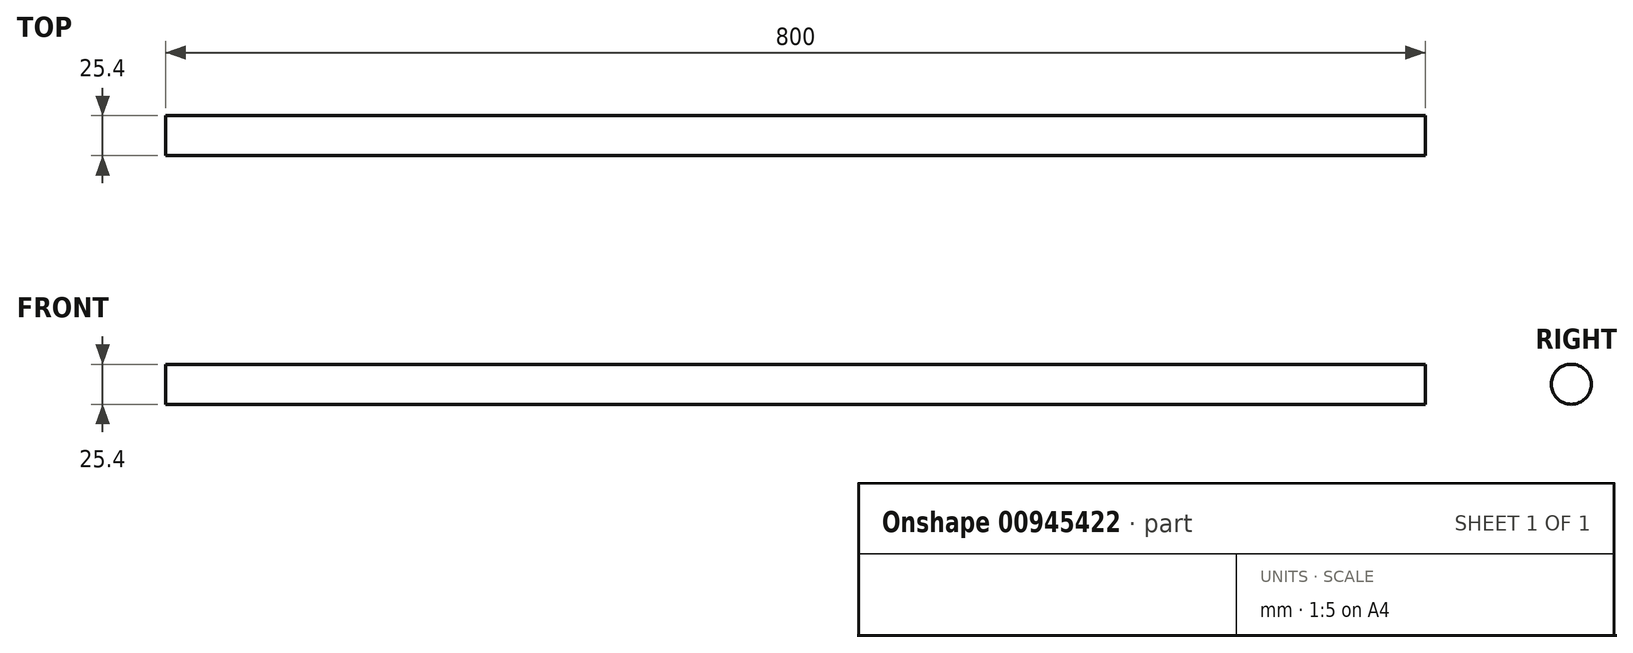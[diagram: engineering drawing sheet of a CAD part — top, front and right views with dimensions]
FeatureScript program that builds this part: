
annotation { "Feature Type Name" : "Feature", "Feature Type Description" : "" }
export const myFeature = defineFeature(function(context is Context, id is Id, definition is map)
    precondition{}
    {
        {
            var Q0;
            Q0=qCreatedBy(makeId("Right.planeOp"),FACE);
            var sketch = newSketch(context, id + "F0", { "sketchPlane" : qUnion([Q0])});
            skCircle(sketch, "E0", {"center": v(0, 0) * mm, "radius": 12.7 * mm});
            skSolve(sketch);
        }
        {
            var Q0;
            Q0=sQuery(id+"F0.wireOp",EDGE,"E0");
            extrude(context, id + "F1", {"bodyType" : ToolBodyType.SURFACE, "surfaceEntities" : qUnion([Q0]), "depth" : 800 * mm, "offsetDistance" : 25.4 * mm});
        }
    });
